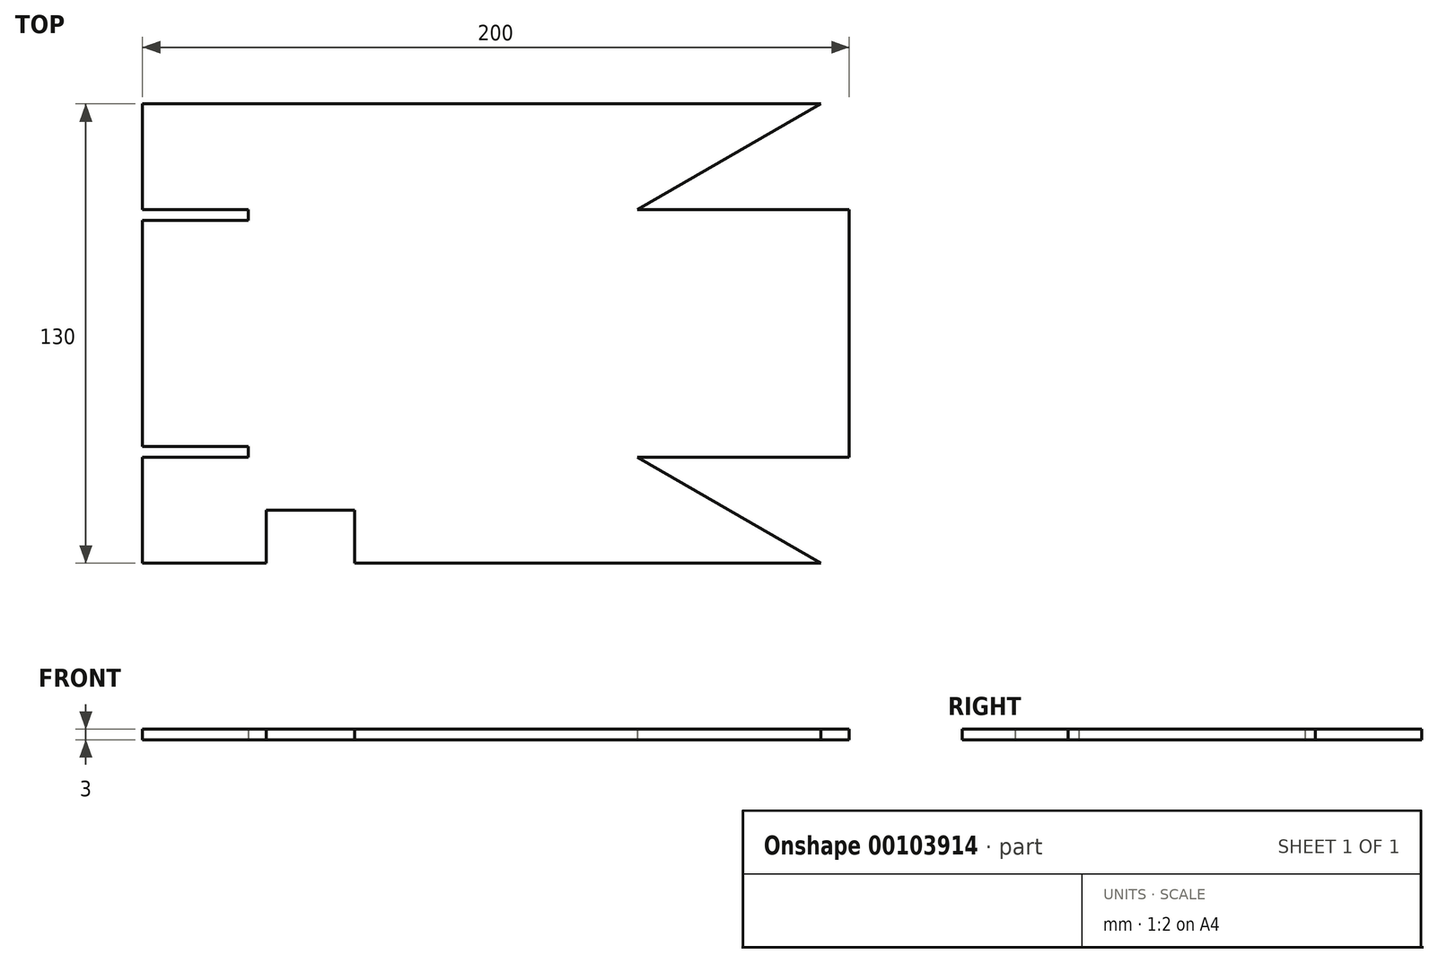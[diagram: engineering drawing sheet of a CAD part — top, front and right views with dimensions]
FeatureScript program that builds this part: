
annotation { "Feature Type Name" : "Feature", "Feature Type Description" : "" }
export const myFeature = defineFeature(function(context is Context, id is Id, definition is map)
    precondition{}
    {
        {
            var Q0;
            Q0=qCreatedBy(makeId("Top.planeOp"),FACE);
            var sketch = newSketch(context, id + "F0", { "sketchPlane" : qUnion([Q0])});
            skLineSegment(sketch, "E0.bottom", {"start": v(-106.09, 79.28) * mm, "end": v(85.87, 79.28) * mm});
            skLineSegment(sketch, "E0.top", {"start": v(-106.09, -50.72) * mm, "end": v(-71.09, -50.72) * mm});
            skLineSegment(sketch, "E0.left", {"start": v(-106.09, 79.28) * mm, "end": v(-106.09, 49.28) * mm});
            skLineSegment(sketch, "E0.right", {"start": v(93.91, 49.28) * mm, "end": v(93.91, -20.72) * mm});
            skLineSegment(sketch, "E1", {"start": v(-106.09, 49.28) * mm, "end": v(93.91, 49.28) * mm});
            skLineSegment(sketch, "E2", {"start": v(-106.09, -20.72) * mm, "end": v(93.91, -20.72) * mm});
            skLineSegment(sketch, "E3", {"start": v(33.91, 49.28) * mm, "end": v(33.91, -20.72) * mm, "construction": true});
            skLineSegment(sketch, "E4", {"start": v(33.91, 49.28) * mm, "end": v(85.87, 79.28) * mm});
            skLineSegment(sketch, "E5", {"start": v(33.91, -20.72) * mm, "end": v(85.87, -50.72) * mm});
            skLineSegment(sketch, "E6", {"start": v(-106.09, 46.28) * mm, "end": v(-76.09, 46.28) * mm});
            skLineSegment(sketch, "E7", {"start": v(-106.09, -17.72) * mm, "end": v(-76.09, -17.72) * mm});
            skLineSegment(sketch, "E8", {"start": v(-76.09, -17.72) * mm, "end": v(-76.09, -20.72) * mm});
            skLineSegment(sketch, "E9", {"start": v(-76.09, 46.28) * mm, "end": v(-76.09, 49.28) * mm});
            skLineSegment(sketch, "E10.trimOffspring", {"start": v(-106.09, 46.28) * mm, "end": v(-106.09, -17.72) * mm});
            skLineSegment(sketch, "E11.trimOffspring", {"start": v(-106.09, -20.72) * mm, "end": v(-106.09, -50.72) * mm});
            skLineSegment(sketch, "E12.top", {"start": v(-71.09, -35.72) * mm, "end": v(-46.09, -35.72) * mm});
            skLineSegment(sketch, "E12.left", {"start": v(-71.09, -50.72) * mm, "end": v(-71.09, -35.72) * mm});
            skLineSegment(sketch, "E12.right", {"start": v(-46.09, -50.72) * mm, "end": v(-46.09, -35.72) * mm});
            skLineSegment(sketch, "E13.trimOffspring", {"start": v(-46.09, -50.72) * mm, "end": v(85.87, -50.72) * mm});
            skLineSegment(sketch, "E14", {"start": v(-76.09, 46.28) * mm, "end": v(-76.09, -17.72) * mm, "construction": true});
            skSolve(sketch);
        }
        {
            var Q0;
            {var subQ4=sQuery(id+"F0.wireOp",EDGE,"E0.right");Q0=makeQuery(id+"F0.imprint","IMPRINT",FACE,{"disambiguationData":[TD([[makeQuery(id+"F0.imprint","IMPRINT",EDGE,{"derivedFrom":subQ4}),-1.0]])]});}
            var Q1;
            Q1=makeQuery(id+"F0.imprint","IMPRINT",FACE,{"disambiguationData":[TD([[makeQuery(id+"F0.imprint","IMPRINT",EDGE,{"derivedFrom":sQuery(id+"F0.wireOp",EDGE,"E0.top")}),1.0]])]});
            var Q2;
            Q2=makeQuery(id+"F0.imprint","IMPRINT",FACE,{"disambiguationData":[TD([[makeQuery(id+"F0.imprint","IMPRINT",EDGE,{"derivedFrom":sQuery(id+"F0.wireOp",EDGE,"E0.bottom")}),-1.0]])]});
            extrude(context, id + "F1", {"entities" : qUnion([Q0, Q1, Q2]), "depth" : 3 * mm});
        }
    });
